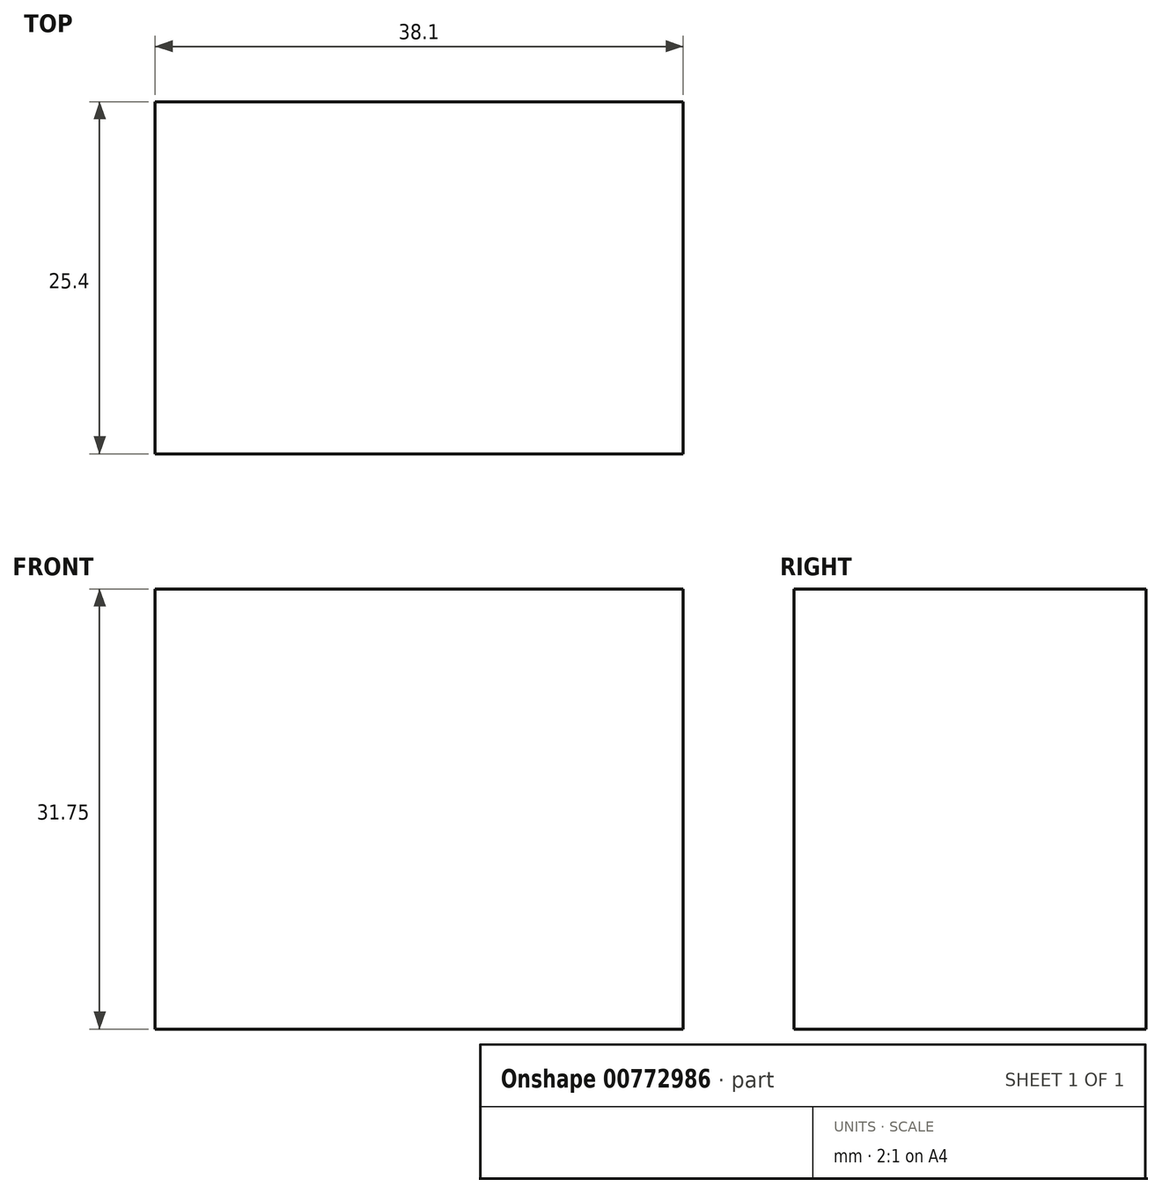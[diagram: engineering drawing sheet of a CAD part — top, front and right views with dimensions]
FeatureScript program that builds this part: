
annotation { "Feature Type Name" : "Feature", "Feature Type Description" : "" }
export const myFeature = defineFeature(function(context is Context, id is Id, definition is map)
    precondition{}
    {
        {
            var Q0;
            Q0=qCreatedBy(makeId("Front.planeOp"),FACE);
            var sketch = newSketch(context, id + "F0", { "sketchPlane" : qUnion([Q0])});
            skLineSegment(sketch, "E0", {"start": v(0, 0) * mm, "end": v(38.1, 0) * mm});
            skLineSegment(sketch, "E1", {"start": v(0, 0) * mm, "end": v(0, 31.75) * mm});
            skLineSegment(sketch, "E2", {"start": v(38.1, 0) * mm, "end": v(38.1, 31.75) * mm});
            skLineSegment(sketch, "E3", {"start": v(38.1, 31.75) * mm, "end": v(0, 31.75) * mm});
            skSolve(sketch);
        }
        {
            var Q0;
            Q0 = qSketchRegion(id + "F0", true);
            extrude(context, id + "F1", {"entities" : qUnion([Q0]), "depth" : 25.4 * mm, "offsetDistance" : 25.4 * mm});
        }
    });
